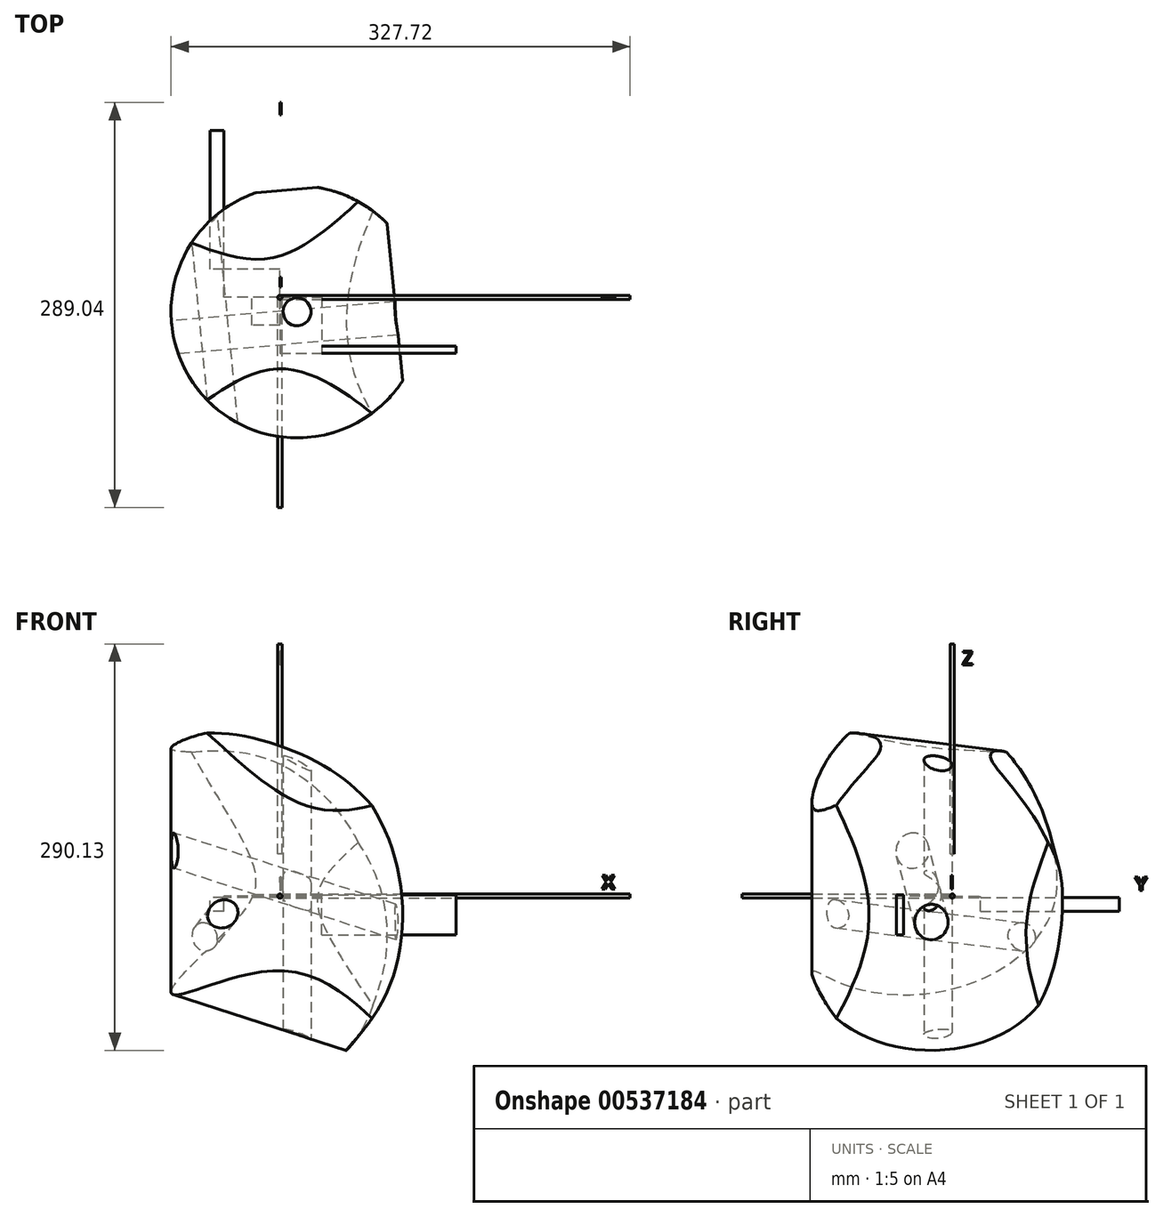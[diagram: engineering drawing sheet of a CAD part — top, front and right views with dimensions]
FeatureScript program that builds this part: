
annotation { "Feature Type Name" : "Feature", "Feature Type Description" : "" }
export const myFeature = defineFeature(function(context is Context, id is Id, definition is map)
    precondition{}
    {
        {
            var Q0;
            Q0=qCreatedBy(makeId("Top.planeOp"),FACE);
            var sketch = newSketch(context, id + "F0", { "sketchPlane" : qUnion([Q0])});
            skLineSegment(sketch, "E0.bottom", {"start": v(0, 0) * mm, "end": v(30, 0) * mm});
            skLineSegment(sketch, "E0.top", {"start": v(0, -40) * mm, "end": v(30, -40) * mm});
            skLineSegment(sketch, "E0.left", {"start": v(0, 0) * mm, "end": v(0, -40) * mm});
            skLineSegment(sketch, "E0.right", {"start": v(30, 0) * mm, "end": v(30, -40) * mm});
            skSolve(sketch);
        }
        {
            var Q0;
            Q0=makeQuery(id+"F0.imprint","IMPRINT",FACE,{"disambiguationData":[TD([[makeQuery(id+"F0.imprint","IMPRINT",EDGE,{"derivedFrom":sQuery(id+"F0.wireOp",EDGE,"E0.bottom")}),-1.0]])]});
            extrude(context, id + "F1", {"entities" : qUnion([Q0]), "depth" : 1 * mm, "offsetDistance" : 25 * mm});
        }
        {
            var Q0;
            Q0=makeQuery(id+"F1.opExtrude","CAP_FACE",FACE,{"disambiguationData":[OSD([sQuery(id+"F0.wireOp",EDGE,"E0.bottom"),sQuery(id+"F0.wireOp",EDGE,"E0.top"),sQuery(id+"F0.wireOp",EDGE,"E0.left"),sQuery(id+"F0.wireOp",EDGE,"E0.right")])],"isStart":false});
            var sketch = newSketch(context, id + "F2", { "sketchPlane" : qUnion([Q0])});
            skLineSegment(sketch, "E1.bottom", {"start": v(30, -40) * mm, "end": v(125.65, -40) * mm});
            skLineSegment(sketch, "E1.top", {"start": v(30, -34.74) * mm, "end": v(125.65, -34.74) * mm});
            skLineSegment(sketch, "E1.left", {"start": v(30, -40) * mm, "end": v(30, -34.74) * mm});
            skLineSegment(sketch, "E1.right", {"start": v(125.65, -40) * mm, "end": v(125.65, -34.74) * mm});
            skSolve(sketch);
        }
        {
            var Q0;
            Q0=makeQuery(id+"F2.imprint","IMPRINT",FACE,{"disambiguationData":[TD([[makeQuery(id+"F2.imprint","IMPRINT",EDGE,{"derivedFrom":sQuery(id+"F2.wireOp",EDGE,"E1.bottom")}),1.0]])]});
            extrude(context, id + "F3", {"entities" : qUnion([Q0]), "oppositeDirection" : true, "depth" : 28.7 * mm, "offsetDistance" : 25 * mm});
        }
        {
            var Q0;
            Q0=makeQuery(id+"F3.opExtrude","CAP_VERTEX",VERTEX,{"disambiguationData":[OSD([sQuery(id+"F0.wireOp",EDGE,"E0.top"),sQuery(id+"F2.wireOp",EDGE,"E1.bottom"),sQuery(id+"F2.wireOp",EDGE,"E1.left")])],"isStart":true});
            var Q1;
            Q1=makeQuery(id+"F3.opExtrude","CAP_VERTEX",VERTEX,{"disambiguationData":[OSD([sQuery(id+"F2.wireOp",EDGE,"E1.top"),sQuery(id+"F2.wireOp",EDGE,"E1.right")])],"isStart":true});
            var Q2;
            Q2=makeQuery(id+"F3.opExtrude","CAP_VERTEX",VERTEX,{"disambiguationData":[OSD([sQuery(id+"F2.wireOp",EDGE,"E1.top"),sQuery(id+"F2.wireOp",EDGE,"E1.right")])],"isStart":false});
            cPlane(context, id + "F4", {"entities" : qUnion([Q0, Q1, Q2]), "cplaneType" : CPlaneType.THREE_POINT, "offset" : 25 * mm, "width" : 150 * mm, "height" : 150 * mm});
        }
        {
            var Q0;
            Q0=qCreatedBy(id+"F4.planeOp",FACE);
            var sketch = newSketch(context, id + "F5", { "sketchPlane" : qUnion([Q0])});
            skLineSegment(sketch, "E2", {"start": v(27.76, 1) * mm, "end": v(123.55, -27.7) * mm});
            skSolve(sketch);
        }
        {
            var Q0;
            Q0=makeQuery(id+"F1.opExtrude","CAP_VERTEX",VERTEX,{"disambiguationData":[OSD([sQuery(id+"F0.wireOp",EDGE,"E0.bottom"),sQuery(id+"F0.wireOp",EDGE,"E0.left")])],"isStart":false});
            var Q1;
            Q1=sQuery(id+"F5.wireOp",VERTEX,"E2.start");
            var Q2;
            Q2=makeQuery(id+"F1.opExtrude","CAP_VERTEX",VERTEX,{"disambiguationData":[OSD([sQuery(id+"F0.wireOp",EDGE,"E0.top"),sQuery(id+"F0.wireOp",EDGE,"E0.right")])],"isStart":true});
            cPlane(context, id + "F6", {"entities" : qUnion([Q0, Q1, Q2]), "cplaneType" : CPlaneType.THREE_POINT, "offset" : 25 * mm, "width" : 150 * mm, "height" : 150 * mm});
        }
        {
            var Q0;
            Q0=qCreatedBy(id+"F6.planeOp",FACE);
            var sketch = newSketch(context, id + "F7", { "sketchPlane" : qUnion([Q0])});
            skLineSegment(sketch, "E3", {"start": v(0, 0) * mm, "end": v(50, 1) * mm});
            skSolve(sketch);
        }
        {
            var Q0;
            Q0=qCreatedBy(makeId("Top.planeOp"),FACE);
            var Q1;
            Q1=sQuery(id+"F5.wireOp",VERTEX,"E2.end");
            cPlane(context, id + "F8", {"entities" : qUnion([Q0, Q1]), "cplaneType" : CPlaneType.PLANE_POINT, "offset" : 25 * mm, "width" : 150 * mm, "height" : 150 * mm});
        }
        {
            var Q0;
            Q0=qCreatedBy(id+"F8.planeOp",FACE);
            var sketch = newSketch(context, id + "F9", { "sketchPlane" : qUnion([Q0])});
            skLineSegment(sketch, "E4.bottom", {"start": v(119.12, -34.74) * mm, "end": v(125.65, -34.74) * mm});
            skLineSegment(sketch, "E4.top", {"start": v(119.12, -15.4) * mm, "end": v(125.65, -15.4) * mm});
            skLineSegment(sketch, "E4.left", {"start": v(125.65, -34.74) * mm, "end": v(125.65, -15.4) * mm});
            skLineSegment(sketch, "E4.right", {"start": v(119.12, -34.74) * mm, "end": v(119.12, -15.4) * mm});
            skLineSegment(sketch, "E5", {"start": v(125.65, -34.74) * mm, "end": v(119.12, -15.4) * mm});
            skSolve(sketch);
        }
        {
            var Q0;
            Q0=sQuery(id+"F9.wireOp",VERTEX,"E4.bottom.start");
            var Q1;
            Q1=sQuery(id+"F2.wireOp",VERTEX,"E1.left.start");
            var Q2;
            Q2=sQuery(id+"F9.wireOp",VERTEX,"E5.end");
            cPlane(context, id + "F10", {"entities" : qUnion([Q0, Q1, Q2]), "cplaneType" : CPlaneType.THREE_POINT, "offset" : 25 * mm, "width" : 150 * mm, "height" : 150 * mm});
        }
        {
            var Q0;
            Q0=qCreatedBy(id+"F10.planeOp",FACE);
            var sketch = newSketch(context, id + "F11", { "sketchPlane" : qUnion([Q0])});
            skLineSegment(sketch, "E6", {"start": v(129.3, -31.83) * mm, "end": v(29.62, -39.9) * mm});
            skLineSegment(sketch, "E7", {"start": v(29.62, -39.9) * mm, "end": v(29.62, -20.1) * mm});
            skLineSegment(sketch, "E8", {"start": v(29.62, -20.1) * mm, "end": v(122.5, -12.59) * mm});
            skLineSegment(sketch, "E9", {"start": v(122.5, -12.59) * mm, "end": v(129.3, -31.83) * mm});
            skSolve(sketch);
        }
        {
            var Q0;
            Q0=sQuery(id+"F11.wireOp",EDGE,"E8");
            var Q1;
            Q1=sQuery(id+"F11.wireOp",VERTEX,"E8.start");
            cPlane(context, id + "F12", {"entities" : qUnion([Q0, Q1]), "cplaneType" : CPlaneType.LINE_POINT, "offset" : 25 * mm, "width" : 150 * mm, "height" : 150 * mm});
        }
        {
            var Q0;
            Q0=qCreatedBy(id+"F12.planeOp",FACE);
            var sketch = newSketch(context, id + "F13", { "sketchPlane" : qUnion([Q0])});
            skCircle(sketch, "E10", {"center": v(-21.8, 7.7) * mm, "radius": 98 * mm});
            skCircle(sketch, "E11", {"center": v(-21.8, 7.7) * mm, "radius": 12 * mm});
            skSolve(sketch);
        }
        {
            var Q0;
            Q0=makeQuery(id+"F13.imprint","IMPRINT",FACE,{"disambiguationData":[TD([[makeQuery(id+"F13.imprint","IMPRINT",EDGE,{"derivedFrom":sQuery(id+"F13.wireOp",EDGE,"E10")}),1.0]])]});
            extrude(context, id + "F14", {"entities" : qUnion([Q0]), "depth" : 100 * mm, "offsetDistance" : 25 * mm, "hasSecondDirection" : true, "secondDirectionOppositeDirection" : true, "secondDirectionDepth" : 250 * mm});
        }
        {
            var Q0;
            Q0=qCreatedBy(makeId("Top.planeOp"),FACE);
            var sketch = newSketch(context, id + "F15", { "sketchPlane" : qUnion([Q0])});
            skLineSegment(sketch, "E12.bottom", {"start": v(0, 0) * mm, "end": v(-20, 0) * mm});
            skLineSegment(sketch, "E12.top", {"start": v(0, -20) * mm, "end": v(-20, -20) * mm});
            skLineSegment(sketch, "E12.left", {"start": v(0, -20) * mm, "end": v(0, 0) * mm});
            skLineSegment(sketch, "E12.right", {"start": v(-20, -20) * mm, "end": v(-20, 0) * mm});
            skSolve(sketch);
        }
        {
            var Q0;
            Q0=makeQuery(id+"F15.imprint","IMPRINT",FACE,{"disambiguationData":[TD([[makeQuery(id+"F15.imprint","IMPRINT",EDGE,{"derivedFrom":sQuery(id+"F15.wireOp",EDGE,"E12.bottom")}),1.0]])]});
            extrude(context, id + "F16", {"entities" : qUnion([Q0]), "depth" : 1 * mm, "offsetDistance" : 25 * mm});
        }
        {
            var Q0;
            Q0=makeQuery(id+"F16.opExtrude","SWEPT_FACE",FACE,{"disambiguationData":[OSD([sQuery(id+"F15.wireOp",EDGE,"E12.right")])]});
            var sketch = newSketch(context, id + "F17", { "sketchPlane" : qUnion([Q0])});
            skLineSegment(sketch, "E13.bottom", {"start": v(0, 1) * mm, "end": v(20, 1) * mm});
            skLineSegment(sketch, "E13.top", {"start": v(0, 65.02) * mm, "end": v(20, 65.02) * mm});
            skLineSegment(sketch, "E13.left", {"start": v(0, 1) * mm, "end": v(0, 65.02) * mm});
            skLineSegment(sketch, "E13.right", {"start": v(20, 1) * mm, "end": v(20, 65.02) * mm});
            skSolve(sketch);
        }
        {
            var Q0;
            Q0=qCreatedBy(makeId("Top.planeOp"),FACE);
            var Q1;
            Q1=sQuery(id+"F17.wireOp",VERTEX,"E13.top.end");
            cPlane(context, id + "F18", {"entities" : qUnion([Q0, Q1]), "cplaneType" : CPlaneType.PLANE_POINT, "offset" : 25 * mm, "width" : 150 * mm, "height" : 150 * mm});
        }
        {
            var Q0;
            Q0=qCreatedBy(id+"F18.planeOp",FACE);
            var sketch = newSketch(context, id + "F19", { "sketchPlane" : qUnion([Q0])});
            skCircle(sketch, "E14", {"center": v(12.28, -10.3) * mm, "radius": 90 * mm});
            skCircle(sketch, "E15", {"center": v(12.28, -10.3) * mm, "radius": 10 * mm});
            skPoint(sketch, "E16.orphan", {"position": v(-20, -20) * mm});
            skSolve(sketch);
        }
        {
            var Q0;
            Q0 = qSketchRegion(id + "F19", true);
            var Q1;
            Q1=makeQuery(id+"F19.imprint","IMPRINT",FACE,{"disambiguationData":[TD([[makeQuery(id+"F19.imprint","IMPRINT",EDGE,{"derivedFrom":sQuery(id+"F19.wireOp",EDGE,"E14")}),1.0]])]});
            extrude(context, id + "F20", {"entities" : qUnion([Q0, Q1]), "depth" : 150 * mm, "offsetDistance" : 25 * mm, "hasSecondDirection" : true, "secondDirectionOppositeDirection" : true, "secondDirectionDepth" : 300 * mm});
        }
        {
            var Q0;
            Q0=qCreatedBy(makeId("Top.planeOp"),FACE);
            var sketch = newSketch(context, id + "F21", { "sketchPlane" : qUnion([Q0])});
            skLineSegment(sketch, "E17.bottom", {"start": v(0, 0) * mm, "end": v(-40, 0) * mm});
            skLineSegment(sketch, "E17.top", {"start": v(0, 20) * mm, "end": v(-40, 20) * mm});
            skLineSegment(sketch, "E17.left", {"start": v(0, 0) * mm, "end": v(0, 20) * mm});
            skLineSegment(sketch, "E17.right", {"start": v(-40, 0) * mm, "end": v(-40, 20) * mm});
            skSolve(sketch);
        }
        {
            var Q0;
            Q0 = qSketchRegion(id + "F21", true);
            extrude(context, id + "F22", {"entities" : qUnion([Q0]), "oppositeDirection" : true, "depth" : 1 * mm, "offsetDistance" : 25 * mm});
        }
        {
            var Q0;
            Q0=makeQuery(id+"F22.opExtrude","CAP_FACE",FACE,{"disambiguationData":[OSD([sQuery(id+"F21.wireOp",EDGE,"E17.bottom"),sQuery(id+"F21.wireOp",EDGE,"E17.top"),sQuery(id+"F21.wireOp",EDGE,"E17.left"),sQuery(id+"F21.wireOp",EDGE,"E17.right")])],"isStart":false});
            var sketch = newSketch(context, id + "F23", { "sketchPlane" : qUnion([Q0])});
            skLineSegment(sketch, "E18.bottom", {"start": v(-40, -20) * mm, "end": v(-49.9, -20) * mm});
            skLineSegment(sketch, "E18.top", {"start": v(-40, -119.01) * mm, "end": v(-49.9, -119.01) * mm});
            skLineSegment(sketch, "E18.left", {"start": v(-40, -20) * mm, "end": v(-40, -119.01) * mm});
            skLineSegment(sketch, "E18.right", {"start": v(-49.9, -20) * mm, "end": v(-49.9, -119.01) * mm});
            skSolve(sketch);
        }
        {
            var Q0;
            Q0 = qSketchRegion(id + "F23", true);
            extrude(context, id + "F24", {"entities" : qUnion([Q0]), "depth" : 9.9 * mm, "offsetDistance" : 25 * mm});
        }
        {
            var Q0;
            Q0=makeQuery(id+"F22.opExtrude","CAP_VERTEX",VERTEX,{"disambiguationData":[OSD([sQuery(id+"F21.wireOp",EDGE,"E17.top"),sQuery(id+"F21.wireOp",EDGE,"E17.right")])],"isStart":false});
            var Q1;
            Q1=makeQuery(id+"F24.opExtrude","CAP_VERTEX",VERTEX,{"disambiguationData":[OSD([sQuery(id+"F23.wireOp",EDGE,"E18.bottom"),sQuery(id+"F23.wireOp",EDGE,"E18.right")])],"isStart":true});
            var Q2;
            Q2=makeQuery(id+"F24.opExtrude","CAP_VERTEX",VERTEX,{"disambiguationData":[OSD([sQuery(id+"F23.wireOp",EDGE,"E18.top"),sQuery(id+"F23.wireOp",EDGE,"E18.right")])],"isStart":false});
            cPlane(context, id + "F25", {"entities" : qUnion([Q0, Q1, Q2]), "cplaneType" : CPlaneType.THREE_POINT, "offset" : 25 * mm, "width" : 150 * mm, "height" : 150 * mm});
        }
        {
            var Q0;
            Q0=qCreatedBy(id+"F25.planeOp",FACE);
            var sketch = newSketch(context, id + "F26", { "sketchPlane" : qUnion([Q0])});
            skLineSegment(sketch, "E19", {"start": v(-40, 20) * mm, "end": v(-49.9, 119.5) * mm});
            skSolve(sketch);
        }
        {
            var Q0;
            Q0=makeQuery(id+"F24.opExtrude","CAP_FACE",FACE,{"disambiguationData":[OSD([sQuery(id+"F23.wireOp",EDGE,"E18.bottom"),sQuery(id+"F23.wireOp",EDGE,"E18.top"),sQuery(id+"F23.wireOp",EDGE,"E18.left"),sQuery(id+"F23.wireOp",EDGE,"E18.right")])],"isStart":false});
            cPlane(context, id + "F27", {"entities" : qUnion([Q0]), "cplaneType" : CPlaneType.OFFSET, "offset" : 0 * mm, "width" : 150 * mm, "height" : 150 * mm});
        }
        {
            var Q0;
            Q0=qCreatedBy(id+"F27.planeOp",FACE);
            var sketch = newSketch(context, id + "F28", { "sketchPlane" : qUnion([Q0])});
            skLineSegment(sketch, "E20.bottom", {"start": v(-58.9, -103.5) * mm, "end": v(-49.9, -103.5) * mm});
            skLineSegment(sketch, "E20.top", {"start": v(-58.9, -119.01) * mm, "end": v(-49.9, -119.01) * mm});
            skLineSegment(sketch, "E20.left", {"start": v(-49.9, -119.01) * mm, "end": v(-49.9, -103.5) * mm});
            skLineSegment(sketch, "E20.right", {"start": v(-58.9, -119.01) * mm, "end": v(-58.9, -103.5) * mm});
            skSolve(sketch);
        }
        {
            var Q0;
            Q0=sQuery(id+"F28.wireOp",VERTEX,"E20.left.end");
            var Q1;
            Q1=sQuery(id+"F28.wireOp",VERTEX,"E20.right.start");
            var Q2;
            Q2=sQuery(id+"F26.wireOp",VERTEX,"E19.start");
            cPlane(context, id + "F29", {"entities" : qUnion([Q0, Q1, Q2]), "cplaneType" : CPlaneType.THREE_POINT, "offset" : 25 * mm, "width" : 150 * mm, "height" : 150 * mm});
        }
        {
            var Q0;
            Q0=qCreatedBy(id+"F29.planeOp",FACE);
            var sketch = newSketch(context, id + "F30", { "sketchPlane" : qUnion([Q0])});
            skLineSegment(sketch, "E21", {"start": v(-58.57, -104.05) * mm, "end": v(-50.83, -27.06) * mm});
            skLineSegment(sketch, "E22", {"start": v(-50.83, -27.06) * mm, "end": v(-71.85, -23.74) * mm});
            skLineSegment(sketch, "E23", {"start": v(-71.85, -23.74) * mm, "end": v(-74, -102.38) * mm});
            skLineSegment(sketch, "E24", {"start": v(-74, -102.38) * mm, "end": v(-58.57, -104.05) * mm});
            skSolve(sketch);
        }
        {
            var Q0;
            Q0=sQuery(id+"F30.wireOp",VERTEX,"E22.start");
            var Q1;
            Q1=sQuery(id+"F30.wireOp",EDGE,"E21");
            cPlane(context, id + "F31", {"entities" : qUnion([Q0, Q1]), "cplaneType" : CPlaneType.LINE_POINT, "offset" : 25 * mm, "width" : 150 * mm, "height" : 150 * mm});
        }
        {
            var Q0;
            Q0=qCreatedBy(id+"F31.planeOp",FACE);
            var sketch = newSketch(context, id + "F32", { "sketchPlane" : qUnion([Q0])});
            skCircle(sketch, "E25", {"center": v(-48.3, -22.8) * mm, "radius": 130 * mm});
            skCircle(sketch, "E26", {"center": v(-48.3, -22.8) * mm, "radius": 10 * mm});
            skSolve(sketch);
        }
        {
            var Q0;
            Q0=makeQuery(id+"F32.imprint","IMPRINT",FACE,{"disambiguationData":[TD([[makeQuery(id+"F32.imprint","IMPRINT",EDGE,{"derivedFrom":sQuery(id+"F32.wireOp",EDGE,"E25")}),1.0]])]});
            extrude(context, id + "F33", {"entities" : qUnion([Q0]), "depth" : 200 * mm, "offsetDistance" : 25 * mm, "hasSecondDirection" : true, "secondDirectionOppositeDirection" : true, "secondDirectionDepth" : 50 * mm});
        }
        {
            var Q0;
            Q0=makeQuery(id+"F14.opExtrude","SWEPT_BODY",BODY,{"disambiguationData":[OSD([sQuery(id+"F13.wireOp",EDGE,"E10"),sQuery(id+"F13.wireOp",EDGE,"E11")])]});
            var Q1;
            Q1=makeQuery(id+"F33.opExtrude","SWEPT_BODY",BODY,{"disambiguationData":[OSD([sQuery(id+"F32.wireOp",EDGE,"E25"),sQuery(id+"F32.wireOp",EDGE,"E26")])]});
            booleanBodies(context, id + "F34", {"operationType" : BooleanOperationType.INTERSECTION, "tools" : qUnion([Q0, Q1])});
        }
        {
            var Q0;
            Q0=makeQuery(id+"F34.opBoolean","INTERSECT",BODY,{"derivedFrom":[makeQuery(id+"F14.opExtrude","SWEPT_BODY",BODY,{"disambiguationData":[OSD([sQuery(id+"F13.wireOp",EDGE,"E10"),sQuery(id+"F13.wireOp",EDGE,"E11")])]}),makeQuery(id+"F33.opExtrude","SWEPT_BODY",BODY,{"disambiguationData":[OSD([sQuery(id+"F32.wireOp",EDGE,"E25"),sQuery(id+"F32.wireOp",EDGE,"E26")])]})]});
            var Q1;
            Q1=makeQuery(id+"F20.opExtrude","SWEPT_BODY",BODY,{"disambiguationData":[OSD([sQuery(id+"F19.wireOp",EDGE,"E14"),sQuery(id+"F19.wireOp",EDGE,"E15")])]});
            booleanBodies(context, id + "F35", {"operationType" : BooleanOperationType.INTERSECTION, "tools" : qUnion([Q0, Q1])});
        }
        {
            var Q0;
            Q0=qCreatedBy(makeId("Top.planeOp"),FACE);
            var sketch = newSketch(context, id + "F36", { "sketchPlane" : qUnion([Q0])});
            skLineSegment(sketch, "E27", {"start": v(0, 0) * mm, "end": v(250, 0) * mm});
            skLineSegment(sketch, "E28", {"start": v(0, 150) * mm, "end": v(0, 0) * mm});
            skSolve(sketch);
        }
        {
            var Q0;
            Q0=sQuery(id+"F36.wireOp",EDGE,"E27");
            var Q1;
            Q1=sQuery(id+"F36.wireOp",VERTEX,"E27.end");
            cPlane(context, id + "F37", {"entities" : qUnion([Q0, Q1]), "cplaneType" : CPlaneType.LINE_POINT, "offset" : 25 * mm, "width" : 150 * mm, "height" : 150 * mm});
        }
        {
            var Q0;
            Q0=qCreatedBy(id+"F37.planeOp",FACE);
            var sketch = newSketch(context, id + "F38", { "sketchPlane" : qUnion([Q0])});
            skCircle(sketch, "E29", {"center": v(0, 0) * mm, "radius": 1.5 * mm});
            skSolve(sketch);
        }
        {
            var Q0;
            Q0=makeQuery(id+"F38.imprint","IMPRINT",FACE,{"disambiguationData":[TD([[makeQuery(id+"F38.imprint","IMPRINT",EDGE,{"derivedFrom":sQuery(id+"F38.wireOp",EDGE,"E29")}),1.0]])]});
            extrude(context, id + "F39", {"entities" : qUnion([Q0]), "oppositeDirection" : true, "depth" : 250 * mm, "offsetDistance" : 25 * mm});
        }
        {
            var Q0;
            Q0=sQuery(id+"F36.wireOp",EDGE,"E28");
            var Q1;
            Q1=sQuery(id+"F36.wireOp",VERTEX,"E28.end");
            cPlane(context, id + "F40", {"entities" : qUnion([Q0, Q1]), "cplaneType" : CPlaneType.LINE_POINT, "offset" : 25 * mm, "width" : 150 * mm, "height" : 150 * mm});
        }
        {
            var Q0;
            Q0=qCreatedBy(id+"F40.planeOp",FACE);
            var sketch = newSketch(context, id + "F41", { "sketchPlane" : qUnion([Q0])});
            skCircle(sketch, "E30", {"center": v(0, 0) * mm, "radius": 1.5 * mm});
            skSolve(sketch);
        }
        {
            var Q0;
            Q0 = qSketchRegion(id + "F41", true);
            extrude(context, id + "F42", {"entities" : qUnion([Q0]), "depth" : 150 * mm, "offsetDistance" : 25 * mm});
        }
        {
            var Q0;
            Q0=qCreatedBy(makeId("Right.planeOp"),FACE);
            var sketch = newSketch(context, id + "F43", { "sketchPlane" : qUnion([Q0])});
            skLineSegment(sketch, "E31", {"start": v(0, 0) * mm, "end": v(0, 180) * mm});
            skSolve(sketch);
        }
        {
            var Q0;
            Q0=sQuery(id+"F43.wireOp",VERTEX,"E31.end");
            var Q1;
            Q1=sQuery(id+"F43.wireOp",EDGE,"E31");
            cPlane(context, id + "F44", {"entities" : qUnion([Q0, Q1]), "cplaneType" : CPlaneType.LINE_POINT, "offset" : 25 * mm, "width" : 150 * mm, "height" : 150 * mm});
        }
        {
            var Q0;
            Q0=qCreatedBy(id+"F44.planeOp",FACE);
            var sketch = newSketch(context, id + "F45", { "sketchPlane" : qUnion([Q0])});
            skCircle(sketch, "E32", {"center": v(0, 0) * mm, "radius": 1.5 * mm});
            skSolve(sketch);
        }
        {
            var Q0;
            Q0=makeQuery(id+"F45.imprint","IMPRINT",FACE,{"disambiguationData":[TD([[makeQuery(id+"F45.imprint","IMPRINT",EDGE,{"derivedFrom":sQuery(id+"F45.wireOp",EDGE,"E32")}),1.0]])]});
            extrude(context, id + "F46", {"entities" : qUnion([Q0]), "oppositeDirection" : true, "depth" : 150 * mm, "offsetDistance" : 25 * mm});
        }
        {
            var Q0;
            Q0=qCreatedBy(makeId("Right.planeOp"),FACE);
            var sketch = newSketch(context, id + "F47", { "sketchPlane" : qUnion([Q0])});
            skText(sketch, "E33", { "text": "Y", "fontName": "Arimo-Bold.ttf"});
            skText(sketch, "E34", { "text": "Z", "fontName": "OpenSans-Regular.ttf"});
            const initialGuessF47  = {"E33": [0.13, 0.00416, 1, 0, 0.01], "E34": [0.00688, 0.165, 1, 0, 0.01]};
            skSetInitialGuess(sketch, initialGuessF47);
            skSolve(sketch);
        }
        {
            var Q0;
            Q0 = qSketchRegion(id + "F47", true);
            extrude(context, id + "F48", {"entities" : qUnion([Q0]), "depth" : 1 * mm, "offsetDistance" : 25 * mm});
        }
        {
            var Q0;
            Q0=qCreatedBy(makeId("Front.planeOp"),FACE);
            var sketch = newSketch(context, id + "F49", { "sketchPlane" : qUnion([Q0])});
            skText(sketch, "E35", { "text": "X", "fontName": "OpenSans-Bold.ttf"});
            const initialGuessF49  = {"E35": [0.22984, 0.005, 1, 0, 0.01]};
            skSetInitialGuess(sketch, initialGuessF49);
            skSolve(sketch);
        }
        {
            var Q0;
            Q0 = qSketchRegion(id + "F49", true);
            extrude(context, id + "F50", {"entities" : qUnion([Q0]), "depth" : 1 * mm, "offsetDistance" : 25 * mm});
        }
    });
